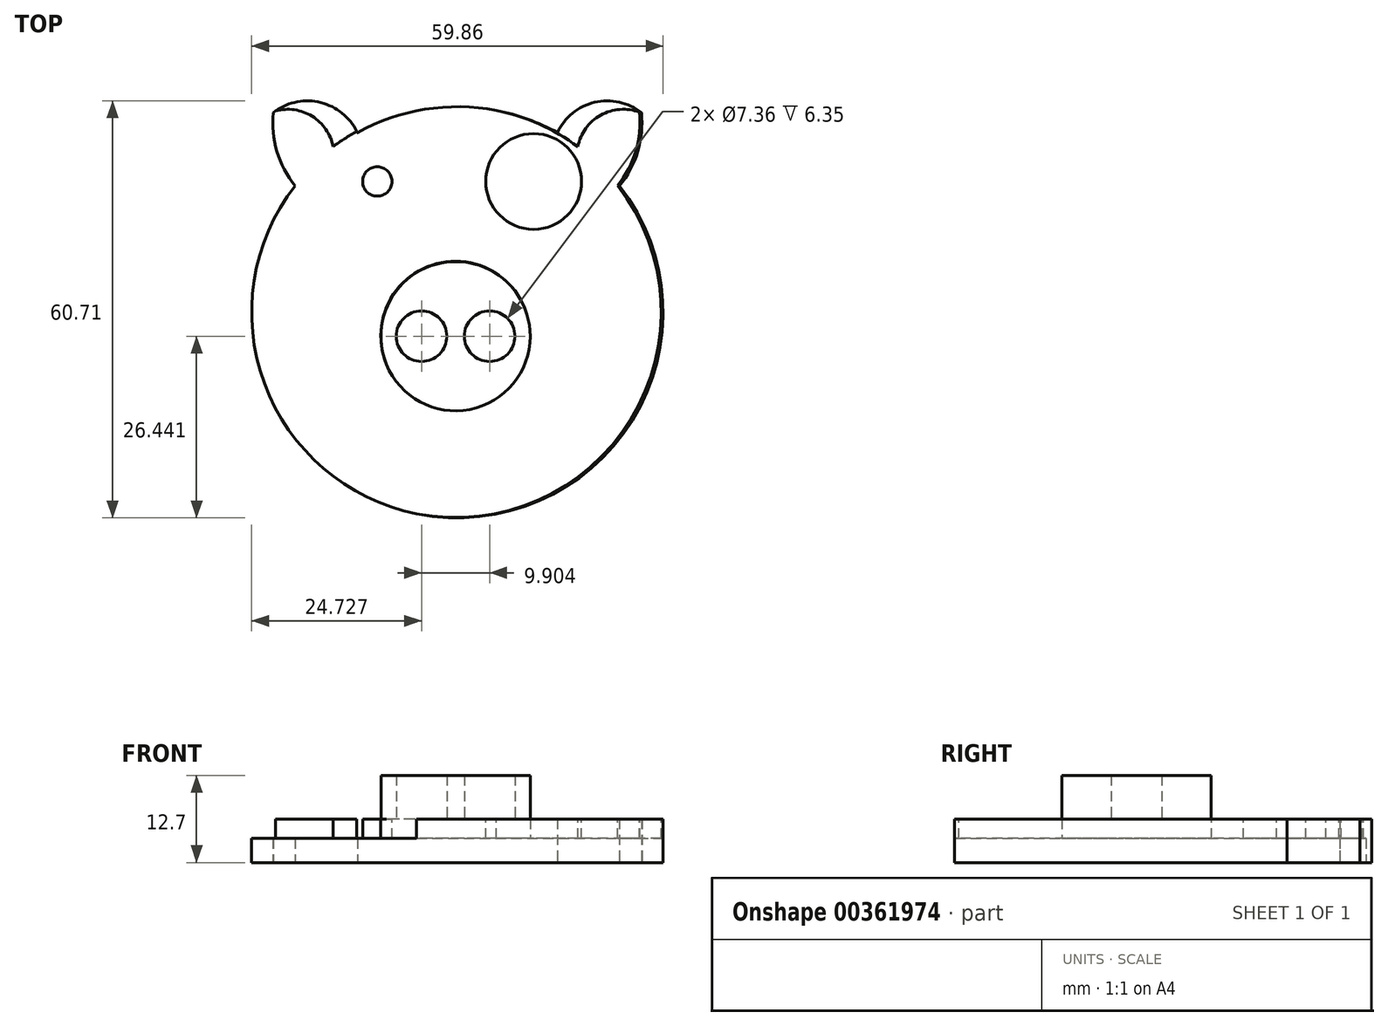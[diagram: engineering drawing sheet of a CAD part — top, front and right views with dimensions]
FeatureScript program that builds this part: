
annotation { "Feature Type Name" : "Feature", "Feature Type Description" : "" }
export const myFeature = defineFeature(function(context is Context, id is Id, definition is map)
    precondition{}
    {
        {
            var Q0;
            Q0=qCreatedBy(makeId("Top.planeOp"),FACE);
            var sketch = newSketch(context, id + "F0", { "sketchPlane" : qUnion([Q0])});
            skArc(sketch, "E0", {"start": v(9.94, 29.64) * mm, "mid": v(-4.6, 33.42) * mm, "end": v(-19.16, 29.64) * mm});
            skArc(sketch, "E1", {"start": v(22.19, 32.54) * mm, "mid": v(15.36, 34.05) * mm, "end": v(9.94, 29.64) * mm});
            skArc(sketch, "E2", {"start": v(18.98, 21.9) * mm, "mid": v(21.64, 26.9) * mm, "end": v(22.19, 32.54) * mm});
            skLineSegment(sketch, "E3", {"start": v(-4.6, 20.27) * mm, "end": v(-4.6, -26.44) * mm, "construction": true});
            skArc(sketch, "E4.MirrorCS", {"start": v(-31.4, 32.54) * mm, "mid": v(-24.58, 34.05) * mm, "end": v(-19.16, 29.64) * mm});
            skArc(sketch, "E5.MirrorCS", {"start": v(-28.2, 21.9) * mm, "mid": v(-30.86, 26.9) * mm, "end": v(-31.4, 32.54) * mm});
            skPoint(sketch, "E6.MirrorCS.end.orphan", {"position": v(22.19, 32.54) * mm});
            skPoint(sketch, "E6.MirrorCS.start.orphan", {"position": v(13.2, 27.54) * mm});
            skPoint(sketch, "E7.start.orphan", {"position": v(-22.42, 27.54) * mm});
            skArc(sketch, "E8.trimOffspring", {"start": v(-28.2, 21.9) * mm, "mid": v(-4.6, -26.44) * mm, "end": v(18.98, 21.9) * mm});
            skSolve(sketch);
        }
        {
            var Q0;
            Q0=makeQuery(id+"F0.imprint","IMPRINT",FACE,{"disambiguationData":[TD([[makeQuery(id+"F0.imprint","IMPRINT",EDGE,{"derivedFrom":sQuery(id+"F0.wireOp",EDGE,"E0")}),1.0]])]});
            extrude(context, id + "F1", {"entities" : qUnion([Q0]), "depth" : 6.35 * mm});
        }
        {
            var Q0;
            Q0=makeQuery(id+"F1.opExtrude","CAP_FACE",FACE,{"disambiguationData":[OSD([sQuery(id+"F0.wireOp",EDGE,"E0"),sQuery(id+"F0.wireOp",EDGE,"E1"),sQuery(id+"F0.wireOp",EDGE,"E2"),sQuery(id+"F0.wireOp",EDGE,"E4.MirrorCS"),sQuery(id+"F0.wireOp",EDGE,"E5.MirrorCS"),sQuery(id+"F0.wireOp",EDGE,"E8.trimOffspring")])],"isStart":false});
            var sketch = newSketch(context, id + "F2", { "sketchPlane" : qUnion([Q0])});
            skLineSegment(sketch, "E9", {"start": v(-4.86, 20.27) * mm, "end": v(-4.86, -26.44) * mm, "construction": true});
            skCircle(sketch, "E10", {"center": v(-4.86, 0) * mm, "radius": 10.86 * mm});
            skCircle(sketch, "E11", {"center": v(-9.81, 0) * mm, "radius": 3.68 * mm});
            skCircle(sketch, "E12.MirrorC", {"center": v(0.1, 0) * mm, "radius": 3.68 * mm});
            skSolve(sketch);
        }
        {
            var Q0;
            Q0=makeQuery(id+"F2.imprint","IMPRINT",FACE,{"disambiguationData":[TD([[makeQuery(id+"F2.imprint","IMPRINT",EDGE,{"derivedFrom":sQuery(id+"F2.wireOp",EDGE,"E10")}),1.0]])]});
            extrude(context, id + "F3", {"entities" : qUnion([Q0]), "operationType" : NewBodyOperationType.ADD, "depth" : 6.35 * mm});
        }
        {
            var Q0;
            {var subQ0=sQuery(id+"F0.wireOp",EDGE,"E2");var subQ1=sQuery(id+"F0.wireOp",EDGE,"E1");var subQ2=sQuery(id+"F0.wireOp",EDGE,"E4.MirrorCS");var subQ3=sQuery(id+"F0.wireOp",EDGE,"E0");var subQ4=sQuery(id+"F0.wireOp",EDGE,"E5.MirrorCS");var subQ5=sQuery(id+"F0.wireOp",EDGE,"E8.trimOffspring");Q0=makeQuery(id+"F3.boolean.opBoolean","SPLIT",FACE,{"disambiguationData":[TD([makeQuery(id+"F1.opExtrude","SWEPT_FACE",FACE,{"disambiguationData":[OSD([subQ3])]})])],"derivedFrom":makeQuery(id+"F1.opExtrude","CAP_FACE",FACE,{"disambiguationData":[OSD([subQ3,subQ1,subQ0,subQ2,subQ4,subQ5])],"isStart":false})});}
            var sketch = newSketch(context, id + "F4", { "sketchPlane" : qUnion([Q0])});
            skCircle(sketch, "E13", {"center": v(-4.88, 3.54) * mm, "radius": 29.93 * mm});
            skArc(sketch, "E14", {"start": v(21.92, 32.6) * mm, "mid": v(15.1, 34.1) * mm, "end": v(9.67, 29.7) * mm});
            skArc(sketch, "E15", {"start": v(18.7, 21.96) * mm, "mid": v(21.37, 26.96) * mm, "end": v(21.92, 32.6) * mm});
            skLineSegment(sketch, "E16", {"start": v(-4.88, 20.32) * mm, "end": v(-4.88, -26.39) * mm, "construction": true});
            skArc(sketch, "E17.MirrorCS", {"start": v(-31.68, 32.6) * mm, "mid": v(-24.86, 34.1) * mm, "end": v(-19.43, 29.7) * mm});
            skArc(sketch, "E18.MirrorCS", {"start": v(-28.47, 21.96) * mm, "mid": v(-31.13, 26.96) * mm, "end": v(-31.68, 32.6) * mm});
            skCircle(sketch, "E19", {"center": v(-16.25, 22.53) * mm, "radius": 6.97 * mm});
            skCircle(sketch, "E20.MirrorC", {"center": v(6.49, 22.53) * mm, "radius": 6.97 * mm});
            skCircle(sketch, "E21", {"center": v(-4.88, 0.05) * mm, "radius": 10.86 * mm});
            skCircle(sketch, "E22", {"center": v(-9.84, 0.05) * mm, "radius": 3.68 * mm});
            skCircle(sketch, "E23.MirrorC", {"center": v(0.07, 0.05) * mm, "radius": 3.68 * mm});
            skCircle(sketch, "E24", {"center": v(-16.25, 22.53) * mm, "radius": 2.14 * mm});
            skCircle(sketch, "E25.MirrorC", {"center": v(6.49, 22.53) * mm, "radius": 2.14 * mm});
            skArc(sketch, "E26", {"start": v(-22.7, 27.6) * mm, "mid": v(-26.02, 32.2) * mm, "end": v(-31.68, 32.6) * mm});
            skArc(sketch, "E27.MirrorCS", {"start": v(12.93, 27.6) * mm, "mid": v(16.25, 32.2) * mm, "end": v(21.92, 32.6) * mm});
            skSolve(sketch);
        }
        {
            var Q0;
            {var subQ0=sQuery(id+"F4.wireOp",EDGE,"E26");var subQ1=sQuery(id+"F4.wireOp",EDGE,"E13");var subQ2=makeQuery(id+"F4.imprint","INTERSECT",VERTEX,{"derivedFrom":[subQ1,subQ0]});Q0=makeQuery(id+"F4.imprint","IMPRINT",FACE,{"disambiguationData":[TD([[makeQuery(id+"F4.imprint","IMPRINT",EDGE,{"disambiguationData":[TD([[subQ2,-1.0]])],"derivedFrom":subQ1}),-1.0]])]});}
            var Q1;
            Q1=makeQuery(id+"F4.imprint","IMPRINT",FACE,{"disambiguationData":[TD([[makeQuery(id+"F4.imprint","IMPRINT",EDGE,{"derivedFrom":sQuery(id+"F4.wireOp",EDGE,"E19")}),1.0]])]});
            var Q2;
            Q2=makeQuery(id+"F4.imprint","IMPRINT",FACE,{"disambiguationData":[TD([[makeQuery(id+"F4.imprint","IMPRINT",EDGE,{"derivedFrom":sQuery(id+"F4.wireOp",EDGE,"E20.MirrorC")}),-1.0]])]});
            var Q3;
            {var subQ0=sQuery(id+"F4.wireOp",EDGE,"E15");Q3=makeQuery(id+"F4.imprint","IMPRINT",FACE,{"disambiguationData":[TD([[makeQuery(id+"F4.imprint","IMPRINT",EDGE,{"derivedFrom":subQ0}),1.0]])]});}
            extrude(context, id + "F5", {"entities" : qUnion([Q0, Q1, Q2, Q3]), "operationType" : NewBodyOperationType.REMOVE, "oppositeDirection" : true, "depth" : 2.84 * mm});
        }
    });
